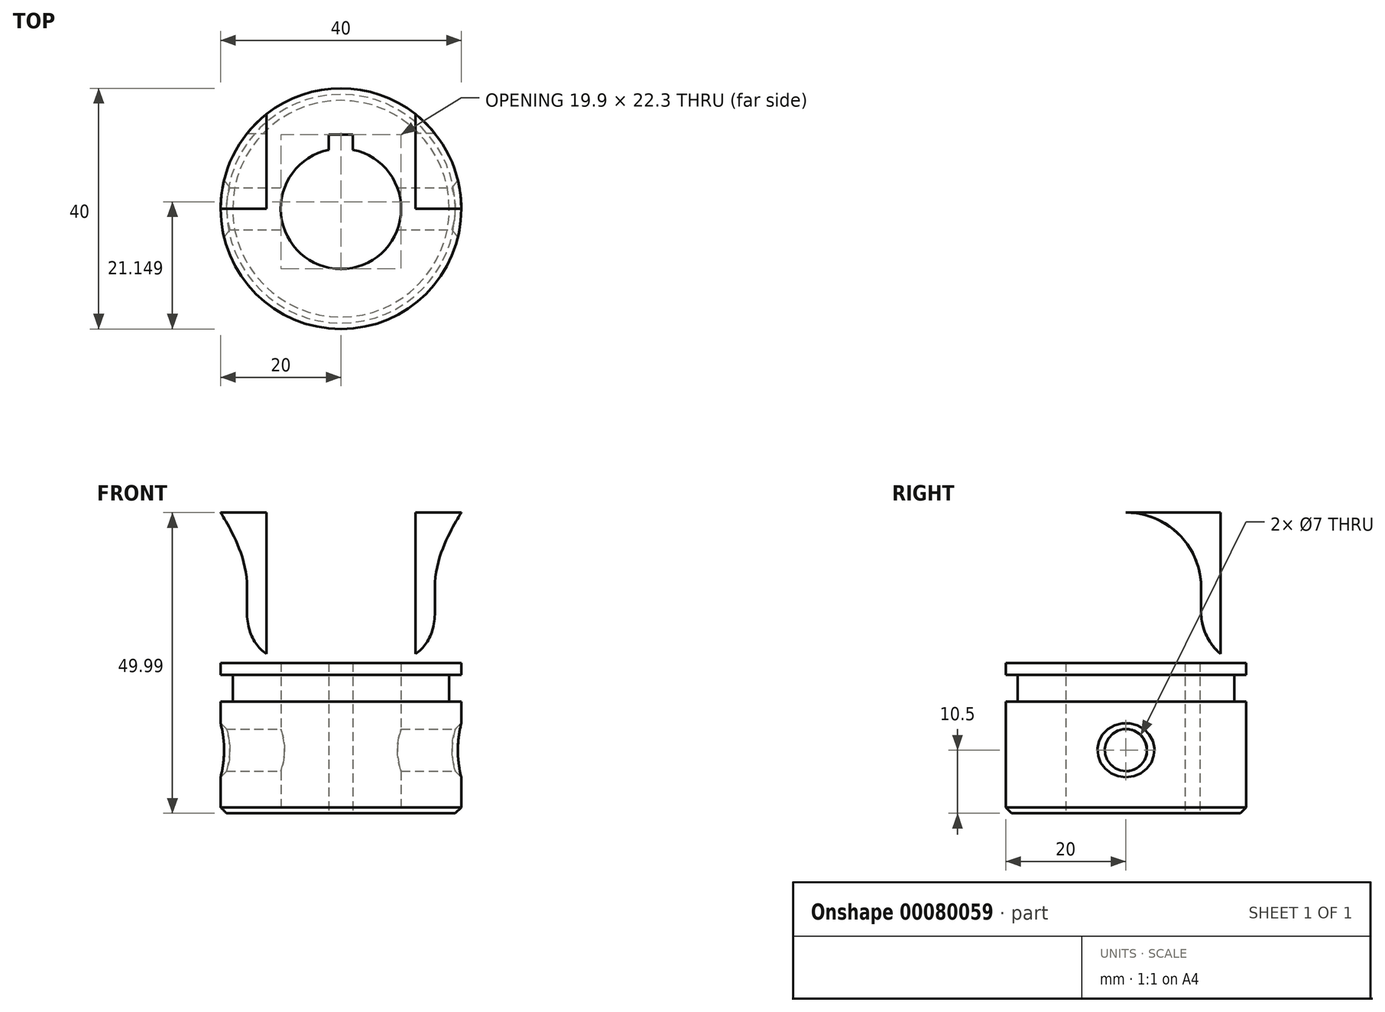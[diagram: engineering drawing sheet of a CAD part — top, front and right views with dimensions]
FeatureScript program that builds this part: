
annotation { "Feature Type Name" : "Feature", "Feature Type Description" : "" }
export const myFeature = defineFeature(function(context is Context, id is Id, definition is map)
    precondition{}
    {
        {
            var Q0;
            Q0=qCreatedBy(makeId("Front.planeOp"),FACE);
            var sketch = newSketch(context, id + "F0", { "sketchPlane" : qUnion([Q0])});
            skLineSegment(sketch, "E0", {"start": v(0, 0) * mm, "end": v(0, 46.72) * mm, "construction": true});
            skLineSegment(sketch, "E1", {"start": v(-10, 0) * mm, "end": v(-20, 0) * mm});
            skLineSegment(sketch, "E2", {"start": v(-20, 0) * mm, "end": v(-20, 18.59) * mm});
            skLineSegment(sketch, "E3", {"start": v(-20, 18.59) * mm, "end": v(-18, 18.59) * mm});
            skLineSegment(sketch, "E4", {"start": v(-18, 18.59) * mm, "end": v(-18, 23) * mm});
            skLineSegment(sketch, "E5", {"start": v(-18, 23) * mm, "end": v(-20, 23) * mm});
            skLineSegment(sketch, "E6", {"start": v(-20, 23) * mm, "end": v(-20, 25) * mm});
            skLineSegment(sketch, "E7", {"start": v(-20, 25) * mm, "end": v(-10, 25) * mm});
            skLineSegment(sketch, "E8", {"start": v(-10, 25) * mm, "end": v(-10, 0) * mm});
            skSolve(sketch);
        }
        {
            var Q0;
            Q0 = qSketchRegion(id + "F0", true);
            var Q1;
            Q1=sQuery(id+"F0.wireOp",EDGE,"E0");
            revolve(context, id + "F1", {"entities" : qUnion([Q0]), "axis" : qUnion([Q1]), "revolveType" : RevolveType.FULL});
        }
        {
            var Q0;
            Q0=qCreatedBy(makeId("Top.planeOp"),FACE);
            var sketch = newSketch(context, id + "F2", { "sketchPlane" : qUnion([Q0])});
            skLineSegment(sketch, "E9", {"start": v(0, 0) * mm, "end": v(0, 24.74) * mm, "construction": true});
            skLineSegment(sketch, "E10", {"start": v(-2, 9.8) * mm, "end": v(-2, 12.3) * mm});
            skLineSegment(sketch, "E11", {"start": v(-2, 12.3) * mm, "end": v(2, 12.3) * mm});
            skLineSegment(sketch, "E12", {"start": v(2, 12.3) * mm, "end": v(2, 9.8) * mm});
            skCircle(sketch, "E13.0", {"center": v(0, 0) * mm, "radius": 10 * mm});
            skCircle(sketch, "E14.0", {"center": v(0, 0) * mm, "radius": 20 * mm});
            skSolve(sketch);
        }
        {
            var Q0;
            {var subQ0=sQuery(id+"F2.wireOp",EDGE,"E10");Q0=makeQuery(id+"F2.imprint","IMPRINT",FACE,{"disambiguationData":[TD([[makeQuery(id+"F2.imprint","IMPRINT",EDGE,{"derivedFrom":subQ0}),-1.0]])]});}
            extrude(context, id + "F3", {"entities" : qUnion([Q0]), "operationType" : NewBodyOperationType.REMOVE, "endBound" : BoundingType.THROUGH_ALL, "depth" : 25 * mm});
        }
        {
            var Q0;
            Q0=makeQuery(id+"F1.opRevolve","SWEPT_FACE",FACE,{"disambiguationData":[OSD([sQuery(id+"F0.wireOp",EDGE,"E7")])]});
            var sketch = newSketch(context, id + "F4", { "sketchPlane" : qUnion([Q0])});
            skLineSegment(sketch, "E15", {"start": v(-12.36, 15.72) * mm, "end": v(-12.36, -15.72) * mm});
            skArc(sketch, "E16.0", {"start": v(-12.36, 15.72) * mm, "mid": v(-20, 0) * mm, "end": v(-12.36, -15.72) * mm});
            skSolve(sketch);
        }
        {
            var Q0;
            Q0 = qSketchRegion(id + "F4", true);
            extrude(context, id + "F5", {"entities" : qUnion([Q0]), "operationType" : NewBodyOperationType.ADD, "depth" : 24.99 * mm});
        }
        {
            var Q0;
            Q0=makeQuery(id+"F5.opExtrude","SWEPT_FACE",FACE,{"disambiguationData":[OSD([sQuery(id+"F4.wireOp",EDGE,"E15")])]});
            var sketch = newSketch(context, id + "F6", { "sketchPlane" : qUnion([Q0])});
            skArc(sketch, "E17", {"start": v(0, 50) * mm, "mid": v(-8.84, 46.33) * mm, "end": v(-12.5, 37.5) * mm});
            skPoint(sketch, "E17.centerSnap0", {"position": v(0, 50) * mm});
            skLineSegment(sketch, "E18", {"start": v(-12.5, 37.5) * mm, "end": v(-12.5, 33.4) * mm});
            skLineSegment(sketch, "E19", {"start": v(0, 37.5) * mm, "end": v(0, 55.9) * mm, "construction": true});
            skPoint(sketch, "E20.visualSharp", {"position": v(-12.5, 24.09) * mm});
            skArc(sketch, "E20.filletArc", {"start": v(-15.72, 26.5) * mm, "mid": v(-13.34, 29.6) * mm, "end": v(-12.5, 33.4) * mm});
            skLineSegment(sketch, "E21", {"start": v(-15.72, 25) * mm, "end": v(-15.72, 26.5) * mm});
            skLineSegment(sketch, "E22", {"start": v(0, 37.5) * mm, "end": v(0, 14.57) * mm});
            skLineSegment(sketch, "E23.MirrorCS", {"start": v(15.72, 25) * mm, "end": v(15.72, 26.5) * mm});
            skPoint(sketch, "E24.MirrorP", {"position": v(12.5, 24.09) * mm});
            skArc(sketch, "E25.MirrorCS", {"start": v(0, 50) * mm, "mid": v(8.84, 46.33) * mm, "end": v(12.5, 37.5) * mm});
            skLineSegment(sketch, "E26.MirrorCS", {"start": v(12.5, 37.5) * mm, "end": v(12.5, 33.4) * mm});
            skArc(sketch, "E27.MirrorCS", {"start": v(15.72, 26.5) * mm, "mid": v(13.34, 29.6) * mm, "end": v(12.5, 33.4) * mm});
            skLineSegment(sketch, "E28", {"start": v(-15.72, 25) * mm, "end": v(15.72, 25) * mm});
            skSolve(sketch);
        }
        {
            var Q0;
            {var subQ8=sQuery(id+"F6.wireOp",EDGE,"E17");Q0=makeQuery(id+"F6.imprint","IMPRINT",FACE,{"disambiguationData":[TD([[makeQuery(id+"F6.imprint","IMPRINT",EDGE,{"derivedFrom":subQ8}),-1.0]])]});}
            var Q1;
            {var subQ8=sQuery(id+"F6.wireOp",EDGE,"E25.MirrorCS");Q1=makeQuery(id+"F6.imprint","IMPRINT",FACE,{"disambiguationData":[TD([[makeQuery(id+"F6.imprint","IMPRINT",EDGE,{"derivedFrom":subQ8}),1.0]])]});}
            extrude(context, id + "F7", {"entities" : qUnion([Q0, Q1]), "operationType" : NewBodyOperationType.REMOVE, "oppositeDirection" : true, "depth" : 25 * mm});
        }
        {
            var Q0;
            Q0=makeQuery(id+"F5.opExtrude","SWEPT_FACE",FACE,{"disambiguationData":[OSD([sQuery(id+"F4.wireOp",EDGE,"E15")])]});
            var sketch = newSketch(context, id + "F8", { "sketchPlane" : qUnion([Q0])});
            skCircle(sketch, "E29", {"center": v(0, 42) * mm, "radius": 5 * mm});
            skSolve(sketch);
        }
        {
            var Q0;
            Q0=makeQuery(id+"F8.imprint","IMPRINT",FACE,{"disambiguationData":[TD([[makeQuery(id+"F8.imprint","IMPRINT",EDGE,{"derivedFrom":sQuery(id+"F8.wireOp",EDGE,"E29")}),1.0]])]});
            extrude(context, id + "F9", {"entities" : qUnion([Q0]), "operationType" : NewBodyOperationType.REMOVE, "endBound" : BoundingType.THROUGH_ALL, "oppositeDirection" : true, "depth" : 25 * mm});
        }
        {
            var Q0;
            Q0=makeQuery(id+"F1.opRevolve","SWEPT_BODY",BODY,{"disambiguationData":[OSD([sQuery(id+"F0.wireOp",EDGE,"E1"),sQuery(id+"F0.wireOp",EDGE,"E2"),sQuery(id+"F0.wireOp",EDGE,"E3"),sQuery(id+"F0.wireOp",EDGE,"E4"),sQuery(id+"F0.wireOp",EDGE,"E5"),sQuery(id+"F0.wireOp",EDGE,"E6"),sQuery(id+"F0.wireOp",EDGE,"E7"),sQuery(id+"F0.wireOp",EDGE,"E8")])]});
            var Q1;
            Q1=qCreatedBy(makeId("Right.planeOp"),FACE);
            mirror(context, id + "F10", {"operationType" : NewBodyOperationType.ADD, "entities" : qUnion([Q0]), "mirrorPlane" : qUnion([Q1])});
        }
        {
            var Q0;
            Q0=qCreatedBy(makeId("Right.planeOp"),FACE);
            var sketch = newSketch(context, id + "F11", { "sketchPlane" : qUnion([Q0])});
            skCircle(sketch, "E30", {"center": v(0, 10.5) * mm, "radius": 3.5 * mm});
            skSolve(sketch);
        }
        {
            var Q0;
            Q0 = qSketchRegion(id + "F11", true);
            extrude(context, id + "F12", {"entities" : qUnion([Q0]), "operationType" : NewBodyOperationType.REMOVE, "endBound" : BoundingType.THROUGH_ALL, "oppositeDirection" : true, "depth" : 25 * mm, "hasSecondDirection" : true, "secondDirectionBound" : SecondDirectionBoundingType.THROUGH_ALL, "secondDirectionOppositeDirection" : false, "secondDirectionDepth" : 25 * mm});
        }
        {
            var Q0;
            Q0=makeQuery(id+"F1.opRevolve","SWEPT_EDGE",EDGE,{"disambiguationData":[OSD([sQuery(id+"F0.wireOp",EDGE,"E1"),sQuery(id+"F0.wireOp",EDGE,"E2")])]});
            var Q1;
            Q1=makeQuery(id+"F12.boolean.opBoolean","INTERSECT",EDGE,{"disambiguationData":[OD(1.0)],"derivedFrom":[makeQuery(id+"F1.opRevolve","SWEPT_FACE",FACE,{"disambiguationData":[OSD([sQuery(id+"F0.wireOp",EDGE,"E2")])]}),makeQuery(id+"F12.opExtrude","SWEPT_FACE",FACE,{"disambiguationData":[OSD([sQuery(id+"F11.wireOp",EDGE,"E30")])]})]});
            var Q2;
            Q2=makeQuery(id+"F10.opPattern","COPY",EDGE,{"derivedFrom":makeQuery(id+"F9.boolean.opBoolean","INTERSECT",EDGE,{"derivedFrom":[makeQuery(id+"F5.boolean.opBoolean","MERGE",FACE,{"derivedFrom":[makeQuery(id+"F1.opRevolve","SWEPT_FACE",FACE,{"disambiguationData":[OSD([sQuery(id+"F0.wireOp",EDGE,"E6")])]}),makeQuery(id+"F5.opExtrude","SWEPT_FACE",FACE,{"disambiguationData":[OSD([sQuery(id+"F4.wireOp",EDGE,"E16.0")])]})]}),makeQuery(id+"F9.opExtrude","SWEPT_FACE",FACE,{"disambiguationData":[OSD([sQuery(id+"F8.wireOp",EDGE,"E29")])]})]}),"instanceName":"1"});
            var Q3;
            Q3=makeQuery(id+"F12.boolean.opBoolean","INTERSECT",EDGE,{"disambiguationData":[OD(0.0)],"derivedFrom":[makeQuery(id+"F1.opRevolve","SWEPT_FACE",FACE,{"disambiguationData":[OSD([sQuery(id+"F0.wireOp",EDGE,"E2")])]}),makeQuery(id+"F12.opExtrude","SWEPT_FACE",FACE,{"disambiguationData":[OSD([sQuery(id+"F11.wireOp",EDGE,"E30")])]})]});
            var Q4;
            Q4=makeQuery(id+"F9.boolean.opBoolean","INTERSECT",EDGE,{"derivedFrom":[makeQuery(id+"F5.boolean.opBoolean","MERGE",FACE,{"derivedFrom":[makeQuery(id+"F1.opRevolve","SWEPT_FACE",FACE,{"disambiguationData":[OSD([sQuery(id+"F0.wireOp",EDGE,"E6")])]}),makeQuery(id+"F5.opExtrude","SWEPT_FACE",FACE,{"disambiguationData":[OSD([sQuery(id+"F4.wireOp",EDGE,"E16.0")])]})]}),makeQuery(id+"F9.opExtrude","SWEPT_FACE",FACE,{"disambiguationData":[OSD([sQuery(id+"F8.wireOp",EDGE,"E29")])]})]});
            chamfer(context, id + "F13", {"entities" : qUnion([Q0, Q1, Q2, Q3, Q4]), "width" : 1 * mm, "tangentPropagation" : true});
        }
    });
